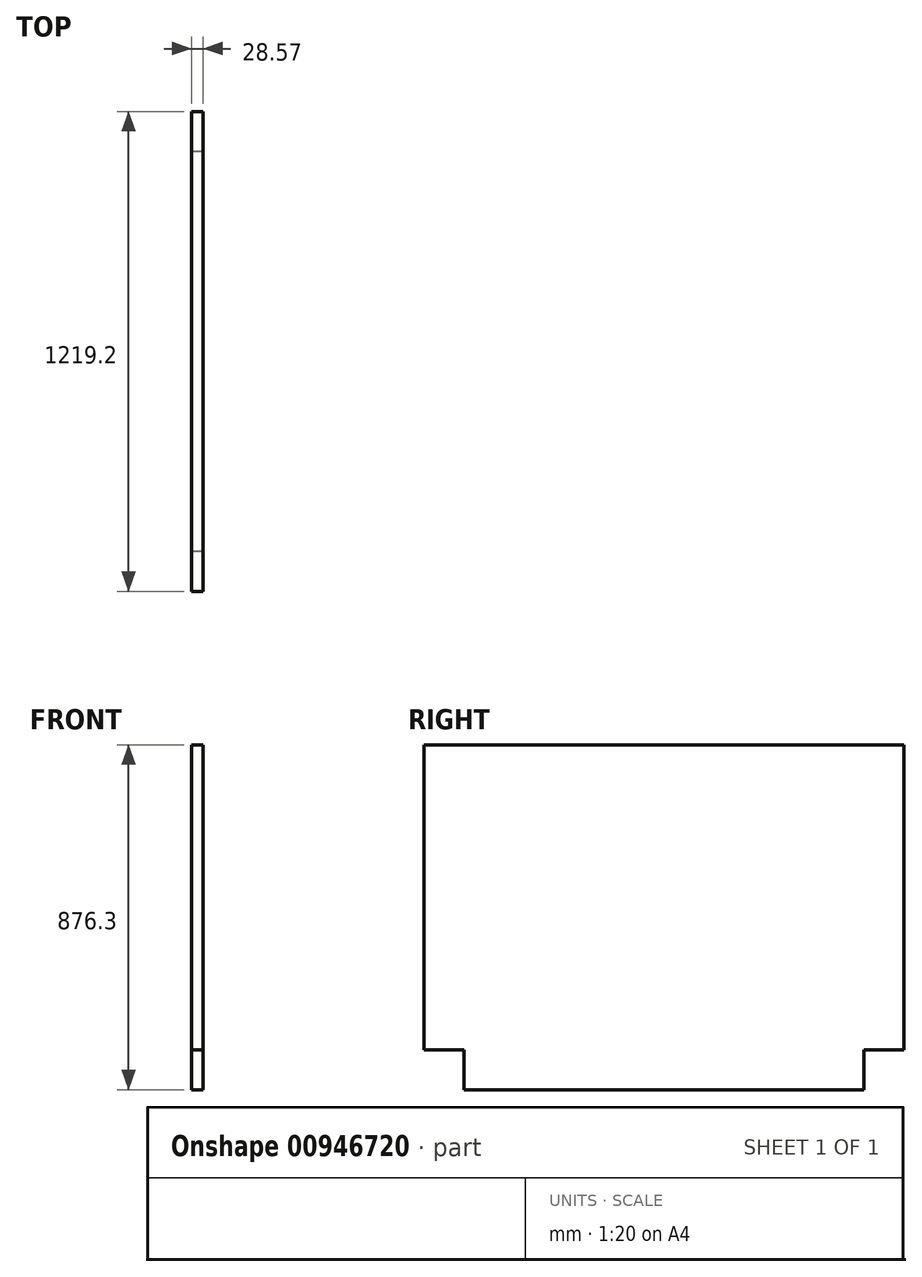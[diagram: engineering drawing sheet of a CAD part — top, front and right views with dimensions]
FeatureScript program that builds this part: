
annotation { "Feature Type Name" : "Feature", "Feature Type Description" : "" }
export const myFeature = defineFeature(function(context is Context, id is Id, definition is map)
    precondition{}
    {
        {
            var Q0;
            Q0=qCreatedBy(makeId("Right.planeOp"),FACE);
            var sketch = newSketch(context, id + "F0", { "sketchPlane" : qUnion([Q0])});
            skLineSegment(sketch, "E0.bottom", {"start": v(609.6, 438.15) * mm, "end": v(-609.6, 438.15) * mm});
            skLineSegment(sketch, "E0.top", {"start": v(609.6, -438.15) * mm, "end": v(-609.6, -438.15) * mm});
            skLineSegment(sketch, "E0.left", {"start": v(609.6, 438.15) * mm, "end": v(609.6, -438.15) * mm});
            skLineSegment(sketch, "E0.right", {"start": v(-609.6, 438.15) * mm, "end": v(-609.6, -438.15) * mm});
            skPoint(sketch, "E0.middle", {"position": v(0, 0) * mm});
            skLineSegment(sketch, "E1.bottom", {"start": v(-609.6, -438.15) * mm, "end": v(-508, -438.15) * mm});
            skLineSegment(sketch, "E1.top", {"start": v(-609.6, -336.55) * mm, "end": v(-508, -336.55) * mm});
            skLineSegment(sketch, "E1.left", {"start": v(-609.6, -438.15) * mm, "end": v(-609.6, -336.55) * mm});
            skLineSegment(sketch, "E1.right", {"start": v(-508, -438.15) * mm, "end": v(-508, -336.55) * mm});
            skLineSegment(sketch, "E2.bottom", {"start": v(609.6, -438.15) * mm, "end": v(508, -438.15) * mm});
            skLineSegment(sketch, "E2.top", {"start": v(609.6, -336.55) * mm, "end": v(508, -336.55) * mm});
            skLineSegment(sketch, "E2.left", {"start": v(609.6, -438.15) * mm, "end": v(609.6, -336.55) * mm});
            skLineSegment(sketch, "E2.right", {"start": v(508, -438.15) * mm, "end": v(508, -336.55) * mm});
            skSolve(sketch);
        }
        {
            var Q0;
            Q0=makeQuery(id+"F0.imprint","IMPRINT",FACE,{"disambiguationData":[TD([[makeQuery(id+"F0.imprint","IMPRINT",EDGE,{"derivedFrom":sQuery(id+"F0.wireOp",EDGE,"E0.bottom")}),1.0]])]});
            extrude(context, id + "F1", {"entities" : qUnion([Q0]), "depth" : 28.57 * mm, "offsetDistance" : 25.4 * mm});
        }
    });
